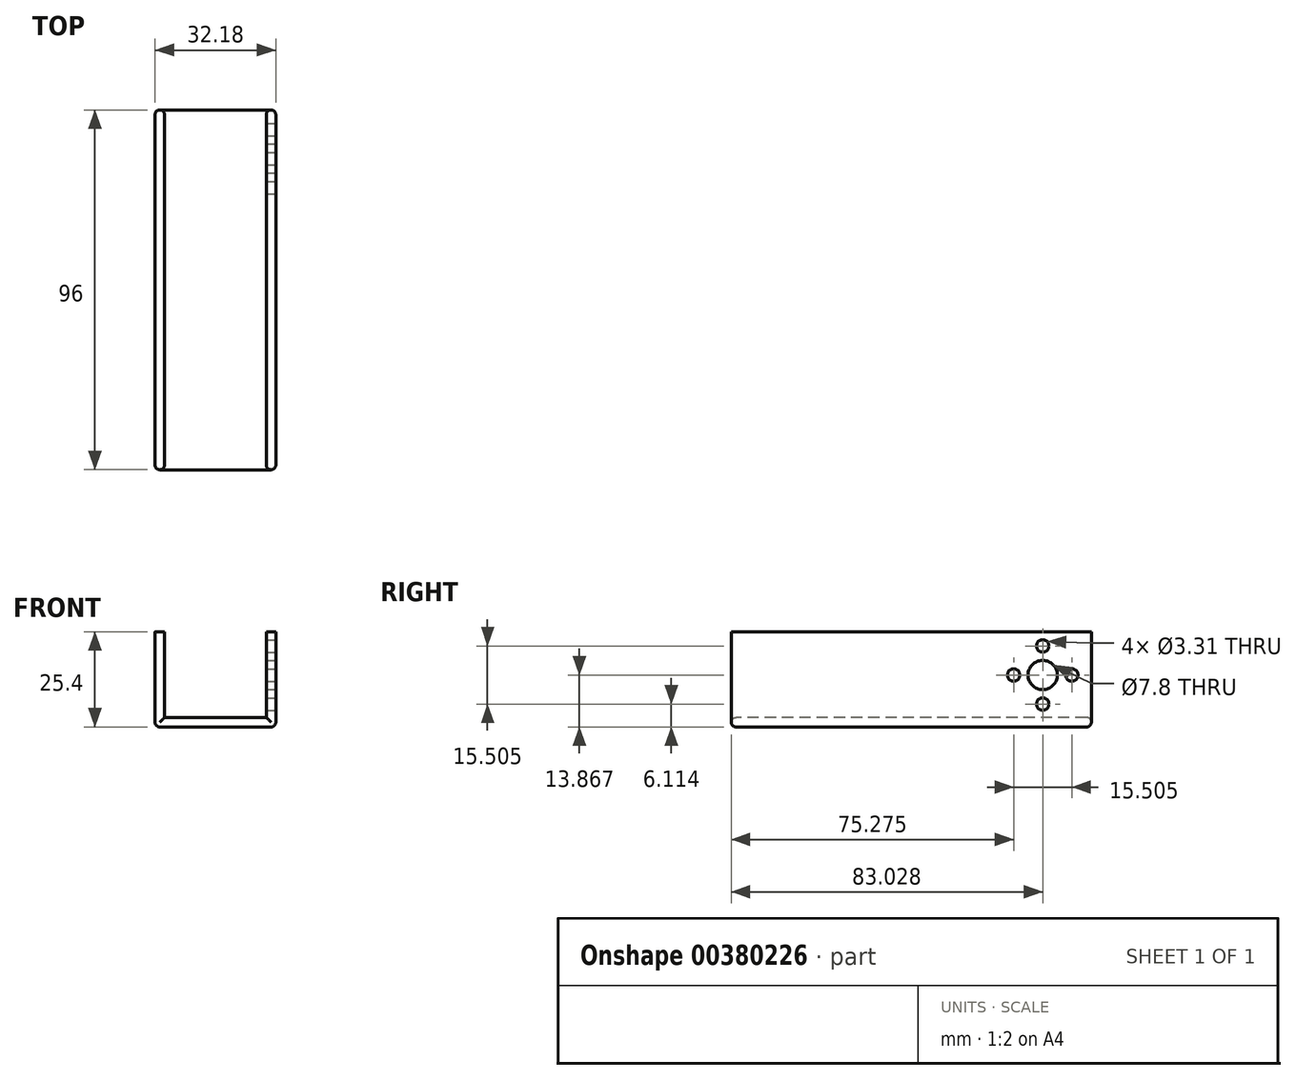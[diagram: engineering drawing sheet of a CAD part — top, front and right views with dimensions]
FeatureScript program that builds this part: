
annotation { "Feature Type Name" : "Feature", "Feature Type Description" : "" }
export const myFeature = defineFeature(function(context is Context, id is Id, definition is map)
    precondition{}
    {
        {
            var Q0;
            Q0=qCreatedBy(makeId("Top.planeOp"),FACE);
            var sketch = newSketch(context, id + "F0", { "sketchPlane" : qUnion([Q0])});
            skLineSegment(sketch, "E0", {"start": v(-32.18, 72.09) * mm, "end": v(-32.18, -23.91) * mm});
            skLineSegment(sketch, "E1", {"start": v(-32.18, -23.91) * mm, "end": v(0, -23.91) * mm});
            skLineSegment(sketch, "E2", {"start": v(0, -23.91) * mm, "end": v(0, 72.09) * mm});
            skLineSegment(sketch, "E3", {"start": v(0, 72.09) * mm, "end": v(-32.18, 72.09) * mm});
            skSolve(sketch);
        }
        {
            var Q0;
            Q0=makeQuery(id+"F0.imprint","IMPRINT",FACE,{"disambiguationData":[TD([[makeQuery(id+"F0.imprint","IMPRINT",EDGE,{"derivedFrom":sQuery(id+"F0.wireOp",EDGE,"E0")}),1.0]])]});
            extrude(context, id + "F1", {"entities" : qUnion([Q0]), "depth" : 25.4 * mm});
        }
        {
            var Q0;
            Q0=makeQuery(id+"F1.opExtrude","SWEPT_FACE",FACE,{"disambiguationData":[OSD([sQuery(id+"F0.wireOp",EDGE,"E1")])]});
            var Q1;
            Q1=makeQuery(id+"F1.opExtrude","SWEPT_FACE",FACE,{"disambiguationData":[OSD([sQuery(id+"F0.wireOp",EDGE,"E3")])]});
            var Q2;
            Q2=makeQuery(id+"F1.opExtrude","CAP_FACE",FACE,{"disambiguationData":[OSD([sQuery(id+"F0.wireOp",EDGE,"E0"),sQuery(id+"F0.wireOp",EDGE,"E1"),sQuery(id+"F0.wireOp",EDGE,"E2"),sQuery(id+"F0.wireOp",EDGE,"E3")])],"isStart":false});
            shell(context, id + "F2", {"entities" : qUnion([Q0, Q1, Q2]), "thickness" : 2.54 * mm});
        }
        {
            var Q0;
            Q0=makeQuery(id+"F1.opExtrude","CAP_EDGE",EDGE,{"disambiguationData":[OSD([sQuery(id+"F0.wireOp",EDGE,"E2")])],"isStart":true});
            var Q1;
            Q1=makeQuery(id+"F1.opExtrude","SWEPT_EDGE",EDGE,{"disambiguationData":[OSD([sQuery(id+"F0.wireOp",EDGE,"E0"),sQuery(id+"F0.wireOp",EDGE,"E1")])]});
            var Q2;
            Q2=makeQuery(id+"F1.opExtrude","SWEPT_EDGE",EDGE,{"disambiguationData":[OSD([sQuery(id+"F0.wireOp",EDGE,"E0"),sQuery(id+"F0.wireOp",EDGE,"E3")])]});
            var Q3;
            Q3=makeQuery(id+"F1.opExtrude","CAP_EDGE",EDGE,{"disambiguationData":[OSD([sQuery(id+"F0.wireOp",EDGE,"E3")])],"isStart":true});
            var Q4;
            Q4=makeQuery(id+"F1.opExtrude","SWEPT_EDGE",EDGE,{"disambiguationData":[OSD([sQuery(id+"F0.wireOp",EDGE,"E1"),sQuery(id+"F0.wireOp",EDGE,"E2")])]});
            fillet(context, id + "F3", {"entities" : qUnion([Q0, Q1, Q2, Q3, Q4]), "radius" : 1.27 * mm, "tangentPropagation" : true, "allowEdgeOverflow" : false});
        }
        {
            var Q0;
            Q0=makeQuery(id+"F1.opExtrude","SWEPT_EDGE",EDGE,{"disambiguationData":[OSD([sQuery(id+"F0.wireOp",EDGE,"E2"),sQuery(id+"F0.wireOp",EDGE,"E3")])]});
            var Q1;
            Q1=makeQuery(id+"F2.opShell","OFFSET_EDGE",EDGE,{"disambiguationData":[OSD([sQuery(id+"F0.wireOp",EDGE,"E2"),sQuery(id+"F0.wireOp",EDGE,"E3")])]});
            var Q2;
            Q2=makeQuery(id+"F2.opShell","OFFSET_EDGE",EDGE,{"disambiguationData":[OSD([sQuery(id+"F0.wireOp",EDGE,"E0"),sQuery(id+"F0.wireOp",EDGE,"E3")])]});
            var Q3;
            Q3=makeQuery(id+"F2.opShell","OFFSET_EDGE",EDGE,{"disambiguationData":[OSD([sQuery(id+"F0.wireOp",EDGE,"E0"),sQuery(id+"F0.wireOp",EDGE,"E1")])]});
            var Q4;
            Q4=makeQuery(id+"F2.opShell","OFFSET_EDGE",EDGE,{"disambiguationData":[OSD([sQuery(id+"F0.wireOp",EDGE,"E1"),sQuery(id+"F0.wireOp",EDGE,"E2")])]});
            fillet(context, id + "F4", {"entities" : qUnion([Q0, Q1, Q2, Q3, Q4]), "radius" : 1.27 * mm, "tangentPropagation" : true, "allowEdgeOverflow" : false});
        }
        {
            var Q0;
            Q0=makeQuery(id+"F1.opExtrude","CAP_EDGE",EDGE,{"disambiguationData":[OSD([sQuery(id+"F0.wireOp",EDGE,"E1")])],"isStart":true});
            var Q1;
            {var subQ0=sQuery(id+"F0.wireOp",EDGE,"E1");Q1=makeQuery(id+"F2.opShell","OFFSET_EDGE",EDGE,{"disambiguationData":[OSD([subQ0]),TDD([makeQuery(id+"F1.opExtrude","CAP_EDGE",EDGE,{"disambiguationData":[OSD([subQ0])],"isStart":true})])]});}
            var Q2;
            {var subQ0=sQuery(id+"F0.wireOp",EDGE,"E3");Q2=makeQuery(id+"F3.opFillet","BLEND_EDGE",EDGE,{"blendedFrom":[makeQuery(id+"F1.opExtrude","CAP_EDGE",EDGE,{"disambiguationData":[OSD([subQ0])],"isStart":true}),makeQuery(id+"F1.opExtrude","CAP_FACE",FACE,{"disambiguationData":[OSD([sQuery(id+"F0.wireOp",EDGE,"E0"),sQuery(id+"F0.wireOp",EDGE,"E1"),sQuery(id+"F0.wireOp",EDGE,"E2"),subQ0])],"isStart":true})],"blendedInto":[makeQuery(id+"F1.opExtrude","CAP_FACE",FACE,{"disambiguationData":[OSD([sQuery(id+"F0.wireOp",EDGE,"E0"),sQuery(id+"F0.wireOp",EDGE,"E1"),sQuery(id+"F0.wireOp",EDGE,"E2"),subQ0])],"isStart":true})]});}
            var Q3;
            {var subQ0=sQuery(id+"F0.wireOp",EDGE,"E3");Q3=makeQuery(id+"F2.opShell","OFFSET_EDGE",EDGE,{"disambiguationData":[OSD([subQ0]),TDD([makeQuery(id+"F1.opExtrude","CAP_EDGE",EDGE,{"disambiguationData":[OSD([subQ0])],"isStart":true})])]});}
            fillet(context, id + "F5", {"entities" : qUnion([Q0, Q1, Q2, Q3]), "radius" : 1.27 * mm, "tangentPropagation" : true, "allowEdgeOverflow" : false});
        }
        {
            var Q0;
            Q0=makeQuery(id+"F1.opExtrude","SWEPT_FACE",FACE,{"disambiguationData":[OSD([sQuery(id+"F0.wireOp",EDGE,"E2")])]});
            var sketch = newSketch(context, id + "F6", { "sketchPlane" : qUnion([Q0])});
            skCircle(sketch, "E4", {"center": v(59.12, 6.11) * mm, "radius": 1.65 * mm});
            skCircle(sketch, "E5", {"center": v(59.12, 13.87) * mm, "radius": 3.9 * mm});
            skLineSegment(sketch, "E6", {"start": v(59.12, 13.87) * mm, "end": v(59.12, 6.11) * mm, "construction": true});
            skCircle(sketch, "E7.cCircle", {"center": v(59.12, 13.87) * mm, "radius": 7.75 * mm, "construction": true});
            skLineSegment(sketch, "E7.0", {"start": v(59.12, 6.11) * mm, "end": v(51.37, 13.87) * mm, "construction": true});
            skLineSegment(sketch, "E7.1", {"start": v(51.37, 13.87) * mm, "end": v(59.12, 21.62) * mm, "construction": true});
            skLineSegment(sketch, "E7.2", {"start": v(59.12, 21.62) * mm, "end": v(66.87, 13.87) * mm, "construction": true});
            skLineSegment(sketch, "E7.3", {"start": v(66.87, 13.87) * mm, "end": v(59.12, 6.11) * mm, "construction": true});
            skCircle(sketch, "E8", {"center": v(51.37, 13.87) * mm, "radius": 1.65 * mm});
            skCircle(sketch, "E9", {"center": v(59.12, 21.62) * mm, "radius": 1.65 * mm});
            skCircle(sketch, "E10", {"center": v(66.87, 13.87) * mm, "radius": 1.65 * mm});
            skSolve(sketch);
        }
        {
            var Q0;
            Q0=makeQuery(id+"F6.imprint","IMPRINT",FACE,{"disambiguationData":[TD([[makeQuery(id+"F6.imprint","IMPRINT",EDGE,{"derivedFrom":sQuery(id+"F6.wireOp",EDGE,"E5")}),1.0]])]});
            var Q1;
            Q1=makeQuery(id+"F6.imprint","IMPRINT",FACE,{"disambiguationData":[TD([[makeQuery(id+"F6.imprint","IMPRINT",EDGE,{"derivedFrom":sQuery(id+"F6.wireOp",EDGE,"E4")}),1.0]])]});
            var Q2;
            Q2=makeQuery(id+"F6.imprint","IMPRINT",FACE,{"disambiguationData":[TD([[makeQuery(id+"F6.imprint","IMPRINT",EDGE,{"derivedFrom":sQuery(id+"F6.wireOp",EDGE,"E10")}),1.0]])]});
            var Q3;
            Q3=makeQuery(id+"F6.imprint","IMPRINT",FACE,{"disambiguationData":[TD([[makeQuery(id+"F6.imprint","IMPRINT",EDGE,{"derivedFrom":sQuery(id+"F6.wireOp",EDGE,"E8")}),1.0]])]});
            var Q4;
            Q4=makeQuery(id+"F6.imprint","IMPRINT",FACE,{"disambiguationData":[TD([[makeQuery(id+"F6.imprint","IMPRINT",EDGE,{"derivedFrom":sQuery(id+"F6.wireOp",EDGE,"E9")}),1.0]])]});
            extrude(context, id + "F7", {"entities" : qUnion([Q0, Q1, Q2, Q3, Q4]), "operationType" : NewBodyOperationType.REMOVE, "oppositeDirection" : true, "depth" : 25.4 * mm});
        }
    });
